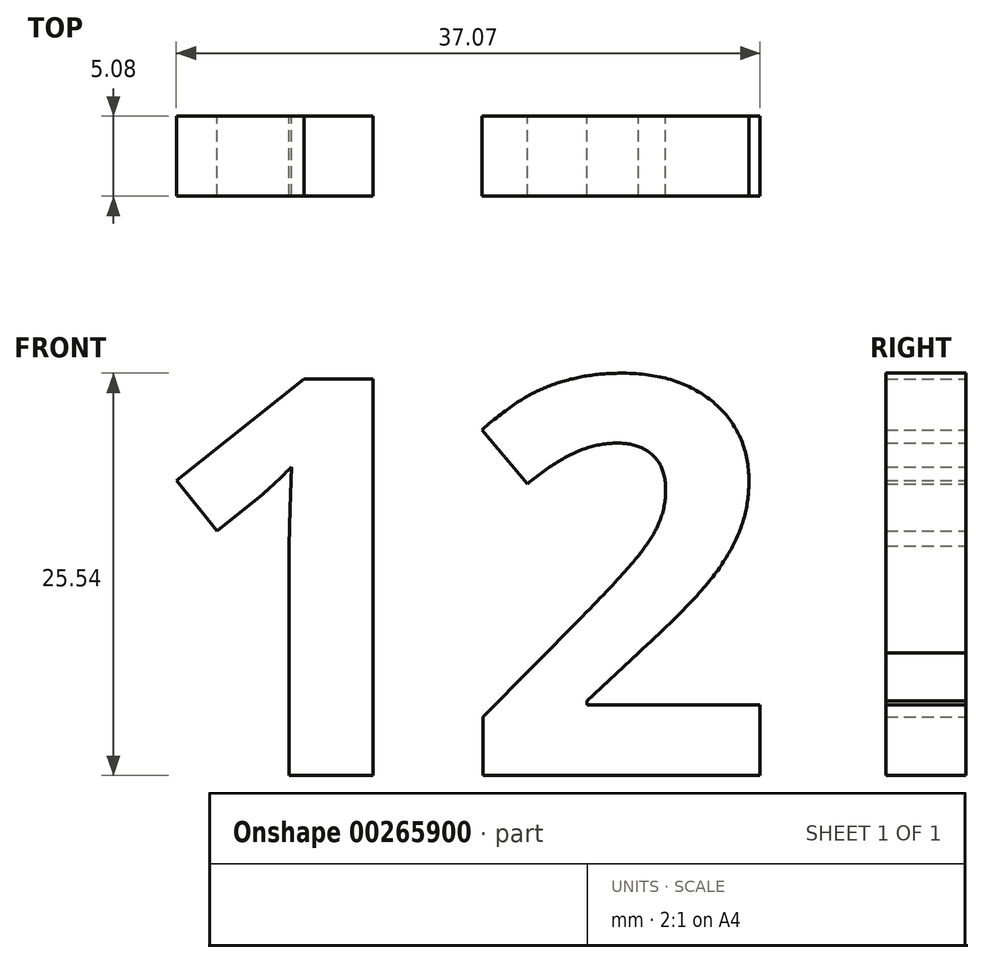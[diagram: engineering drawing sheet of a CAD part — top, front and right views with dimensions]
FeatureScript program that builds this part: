
annotation { "Feature Type Name" : "Feature", "Feature Type Description" : "" }
export const myFeature = defineFeature(function(context is Context, id is Id, definition is map)
    precondition{}
    {
        {
            var Q0;
            Q0=qCreatedBy(makeId("Front.planeOp"),FACE);
            var sketch = newSketch(context, id + "F0", { "sketchPlane" : qUnion([Q0])});
            skText(sketch, "E0", { "text": "12\n", "fontName": "OpenSans-Bold.ttf"});
            const initialGuessF0  = {"E0": [-0.03553, -0.01372, 1, 0, 0.0254]};
            skSetInitialGuess(sketch, initialGuessF0);
            skSolve(sketch);
        }
        {
            var Q0;
            Q0 = qSketchRegion(id + "F0", true);
            extrude(context, id + "F1", {"entities" : qUnion([Q0]), "depth" : 5.08 * mm});
        }
    });
